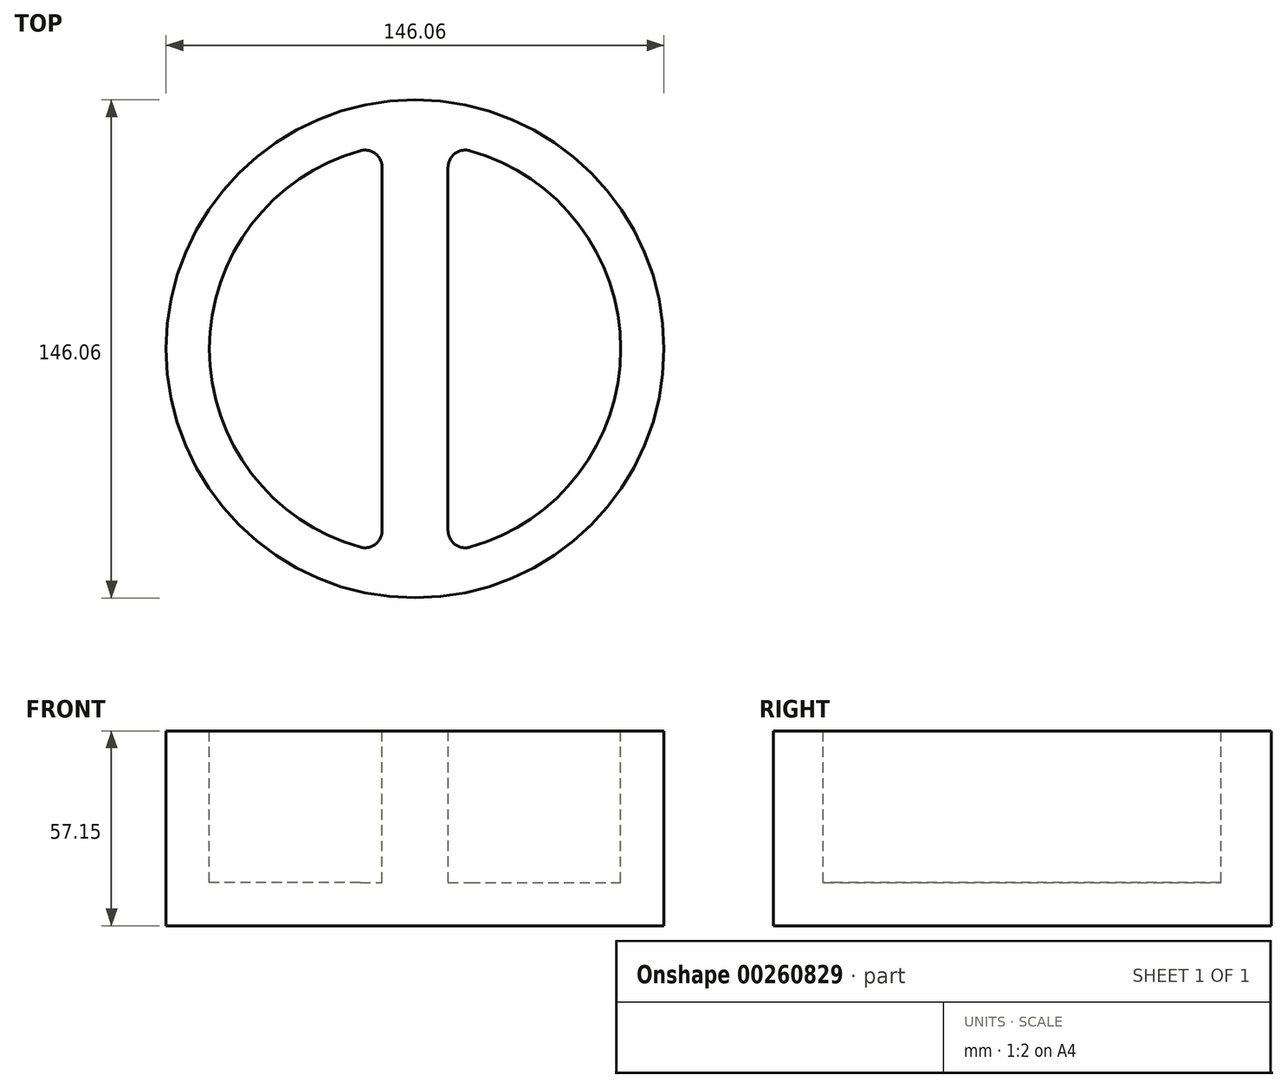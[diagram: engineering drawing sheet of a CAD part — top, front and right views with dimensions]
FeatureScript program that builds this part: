
annotation { "Feature Type Name" : "Feature", "Feature Type Description" : "" }
export const myFeature = defineFeature(function(context is Context, id is Id, definition is map)
    precondition{}
    {
        {
            var Q0;
            Q0=qCreatedBy(makeId("Top.planeOp"),FACE);
            var sketch = newSketch(context, id + "F0", { "sketchPlane" : qUnion([Q0])});
            skCircle(sketch, "E0", {"center": v(0, 0) * mm, "radius": 73.03 * mm});
            skSolve(sketch);
        }
        {
            var Q0;
            Q0 = qSketchRegion(id + "F0", true);
            extrude(context, id + "F1", {"entities" : qUnion([Q0]), "depth" : 57.15 * mm});
        }
        {
            var Q0;
            Q0=makeQuery(id+"F1.opExtrude","CAP_FACE",FACE,{"disambiguationData":[OSD([sQuery(id+"F0.wireOp",EDGE,"E0")])],"isStart":false});
            var sketch = newSketch(context, id + "F2", { "sketchPlane" : qUnion([Q0])});
            skCircle(sketch, "E1", {"center": v(0, 0) * mm, "radius": 60.33 * mm});
            skLineSegment(sketch, "E2", {"start": v(0, 0) * mm, "end": v(-9.65, 0) * mm});
            skLineSegment(sketch, "E3", {"start": v(0, 0) * mm, "end": v(9.65, 0) * mm});
            skLineSegment(sketch, "E4", {"start": v(-9.65, 59.55) * mm, "end": v(-9.65, -59.55) * mm});
            skLineSegment(sketch, "E5", {"start": v(9.65, 59.55) * mm, "end": v(9.65, -59.55) * mm});
            skSolve(sketch);
        }
        {
            var Q0;
            {var subQ0=sQuery(id+"F2.wireOp",EDGE,"E4");var subQ1=sQuery(id+"F2.wireOp",EDGE,"E1");var subQ2=makeQuery(id+"F2.imprint","INTERSECT",VERTEX,{"disambiguationData":[OD(0.0)],"derivedFrom":[subQ1,subQ0]});Q0=makeQuery(id+"F2.imprint","IMPRINT",FACE,{"disambiguationData":[TD([[makeQuery(id+"F2.imprint","IMPRINT",EDGE,{"disambiguationData":[TD([[subQ2,-1.0]])],"derivedFrom":subQ1}),1.0]])]});}
            var Q1;
            {var subQ0=sQuery(id+"F2.wireOp",EDGE,"E5");var subQ1=sQuery(id+"F2.wireOp",EDGE,"E1");var subQ2=makeQuery(id+"F2.imprint","INTERSECT",VERTEX,{"disambiguationData":[OD(0.0)],"derivedFrom":[subQ1,subQ0]});Q1=makeQuery(id+"F2.imprint","IMPRINT",FACE,{"disambiguationData":[TD([[makeQuery(id+"F2.imprint","IMPRINT",EDGE,{"disambiguationData":[TD([[subQ2,1.0]])],"derivedFrom":subQ1}),1.0]])]});}
            extrude(context, id + "F3", {"entities" : qUnion([Q0, Q1]), "operationType" : NewBodyOperationType.REMOVE, "oppositeDirection" : true, "depth" : 44.45 * mm});
        }
        {
            var Q0;
            {var subQ0=sQuery(id+"F2.wireOp",EDGE,"E4");var subQ1=sQuery(id+"F2.wireOp",EDGE,"E1");Q0=makeQuery(id+"F3.boolean.opBoolean","COPY",EDGE,{"derivedFrom":makeQuery(id+"F3.opExtrude","SWEPT_EDGE",EDGE,{"disambiguationData":[OSD([subQ1,subQ0]),TDD([makeQuery(id+"F2.imprint","INTERSECT",VERTEX,{"disambiguationData":[OD(0.0)],"derivedFrom":[subQ1,subQ0]})])]})});}
            fillet(context, id + "F4", {"entities" : qUnion([Q0]), "radius" : 5.08 * mm, "tangentPropagation" : true, "allowEdgeOverflow" : false});
        }
        {
            var Q0;
            {var subQ0=sQuery(id+"F2.wireOp",EDGE,"E5");var subQ1=sQuery(id+"F2.wireOp",EDGE,"E1");Q0=makeQuery(id+"F3.boolean.opBoolean","COPY",EDGE,{"derivedFrom":makeQuery(id+"F3.opExtrude","SWEPT_EDGE",EDGE,{"disambiguationData":[OSD([subQ1,subQ0]),TDD([makeQuery(id+"F2.imprint","INTERSECT",VERTEX,{"disambiguationData":[OD(0.0)],"derivedFrom":[subQ1,subQ0]})])]})});}
            var Q1;
            {var subQ0=sQuery(id+"F2.wireOp",EDGE,"E5");var subQ1=sQuery(id+"F2.wireOp",EDGE,"E1");Q1=makeQuery(id+"F3.boolean.opBoolean","COPY",EDGE,{"derivedFrom":makeQuery(id+"F3.opExtrude","SWEPT_EDGE",EDGE,{"disambiguationData":[OSD([subQ1,subQ0]),TDD([makeQuery(id+"F2.imprint","INTERSECT",VERTEX,{"disambiguationData":[OD(1.0)],"derivedFrom":[subQ1,subQ0]})])]})});}
            var Q2;
            {var subQ0=sQuery(id+"F2.wireOp",EDGE,"E4");var subQ1=sQuery(id+"F2.wireOp",EDGE,"E1");Q2=makeQuery(id+"F3.boolean.opBoolean","COPY",EDGE,{"derivedFrom":makeQuery(id+"F3.opExtrude","SWEPT_EDGE",EDGE,{"disambiguationData":[OSD([subQ1,subQ0]),TDD([makeQuery(id+"F2.imprint","INTERSECT",VERTEX,{"disambiguationData":[OD(1.0)],"derivedFrom":[subQ1,subQ0]})])]})});}
            fillet(context, id + "F5", {"entities" : qUnion([Q0, Q1, Q2]), "radius" : 5.08 * mm, "tangentPropagation" : true, "allowEdgeOverflow" : false});
        }
    });
